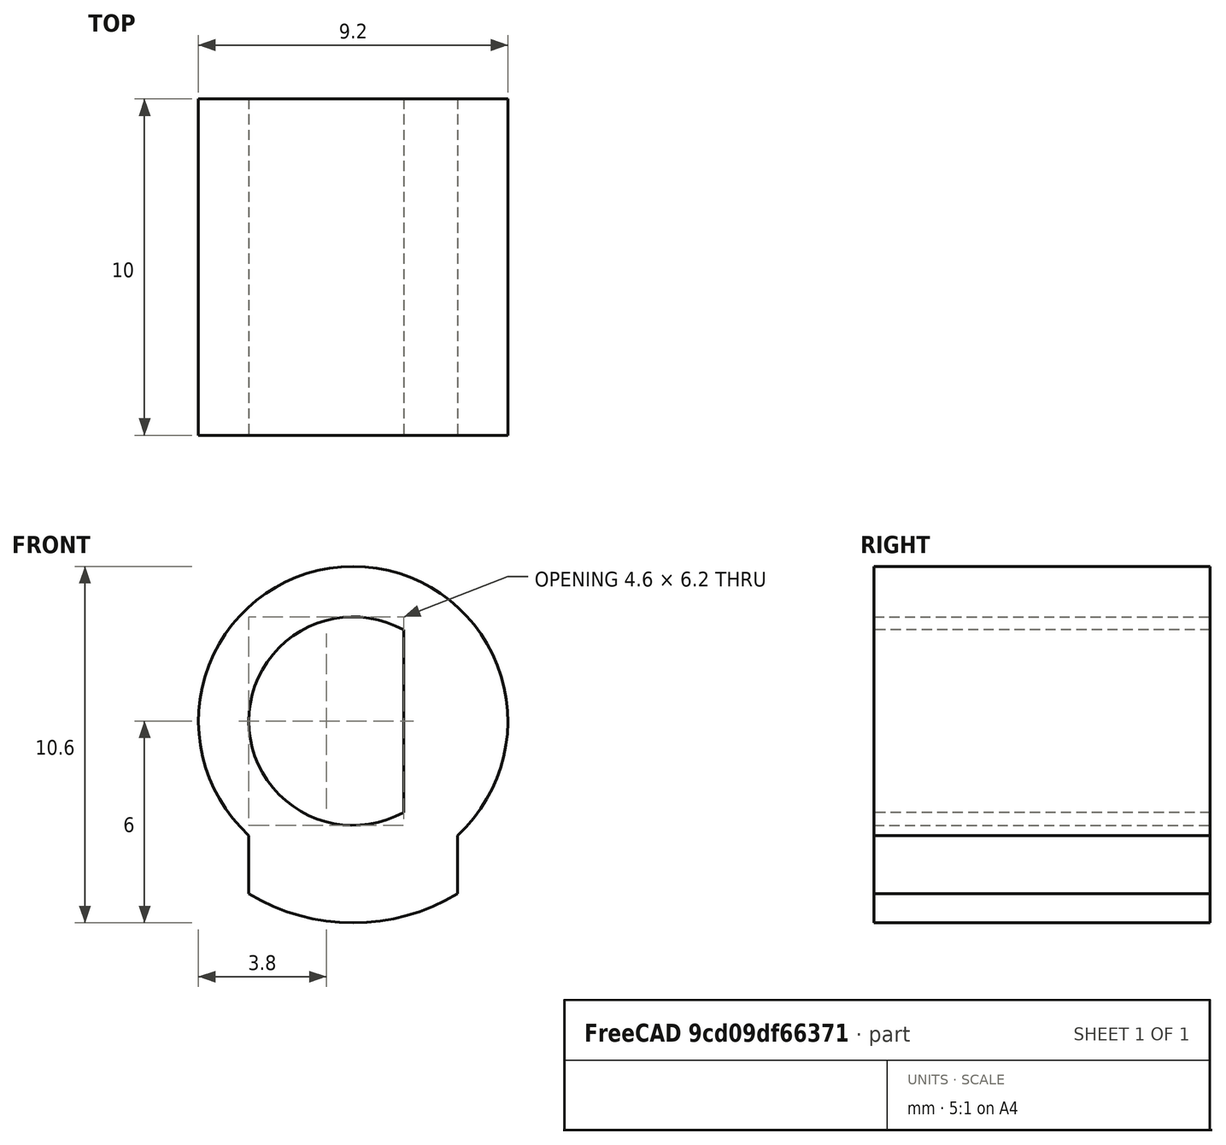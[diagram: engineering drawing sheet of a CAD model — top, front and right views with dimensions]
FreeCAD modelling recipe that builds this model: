
FCSTD DOCUMENT  (FreeCAD 0.19R24276 (Git))
Label: volume_knob
License: All rights reserved
LicenseURL: http://en.wikipedia.org/wiki/All_rights_reserved
objects: Spreadsheet::Sheet×1, Sketcher::SketchObject×1, PartDesign::Pad×1, PartDesign::Body×1
note: 4 computed .brp shape members not serialized (recipe doc carries the construction recipe); baked Part::Feature solids carry a one-line shape summary decoded from their .brp

FEATURE [Spreadsheet::Sheet] Spreadsheet
  cells = A1=overall diam; B1(overall_diam)=12; A2=shaft diam; B2(shaft_diam)=6.2; A3=shaft flat; B3(shaft_flat)=4.6; A4=shaft flat dist; B4(shaft_flat_offset)==shaft_flat - shaft_diam / 2; A5=shaft depth; B5(shaft_depth)=7
FEATURE [Sketcher::SketchObject] Sketch
  FullyConstrained = true
  MapMode = 5
  Placement = pos=(0,0,0) rot=(1,0,0;1.5708rad)
  Support = -> [XZ_Plane]
  expr: Constraints[15] = <<Spreadsheet>>.shaft_diam + 3
  expr: Constraints[9] = <<Spreadsheet>>.overall_diam
  expr: Constraints[7] = <<Spreadsheet>>.shaft_diam
  expr: Constraints[6] = <<Spreadsheet>>.shaft_flat_offset
  sketch-geometry (11):
    g0: Circle CenterX=0 CenterY=0 CenterZ=0 NormalX=0 NormalY=0 NormalZ=1 AngleXU=0 Radius=3.1
    g1: LineSegment StartX=1.5 StartY=2.71293 StartZ=0 EndX=1.5 EndY=-2.71293 EndZ=0
    g2: ArcOfCircle CenterX=0 CenterY=0 CenterZ=0 NormalX=0 NormalY=0 NormalZ=1 AngleXU=0 Radius=3.1 StartAngle=1.06572 EndAngle=5.21746
    g3: Circle CenterX=0 CenterY=0 CenterZ=0 NormalX=0 NormalY=0 NormalZ=1 AngleXU=0 Radius=6
    g4: LineSegment StartX=-3.1 StartY=0 StartZ=0 EndX=-3.1 EndY=-5.13712 EndZ=0
    g5: Circle CenterX=0 CenterY=0 CenterZ=0 NormalX=0 NormalY=0 NormalZ=1 AngleXU=0 Radius=4.6
    g6: LineSegment StartX=-3.1 StartY=-5.13712 StartZ=0 EndX=-3.1 EndY=-3.39853 EndZ=0
    g7: ArcOfCircle CenterX=0 CenterY=0 CenterZ=0 NormalX=0 NormalY=0 NormalZ=1 AngleXU=0 Radius=4.6 StartAngle=5.45188 EndAngle=10.2561
    g8: ArcOfCircle CenterX=0 CenterY=0 CenterZ=0 NormalX=0 NormalY=0 NormalZ=1 AngleXU=0 Radius=6 StartAngle=4.16944 EndAngle=5.25534
    g9: LineSegment StartX=3.1 StartY=5.69007e-08 StartZ=0 EndX=3.1 EndY=-5.13712 EndZ=0
    g10: LineSegment StartX=3.1 StartY=-5.13712 StartZ=0 EndX=3.1 EndY=-3.39853 EndZ=0
  constraints (31):
    c: Coincident(g0,g-1)
    c: PointOnObject(g1,g0)
    c: Vertical(g1)
    c: Coincident(g2,g-1)
    c: Coincident(g2,g1)
    c: Coincident(g2,g1)
    c: DistanceX(g2,g1) = 1.5
    c: Diameter(g0) = 6.2
    c: Coincident(g3,g2)
    c: Diameter(g3) = 12
    c: PointOnObject(g4,g2)
    c: PointOnObject(g4,g3)
    c: Vertical(g4)
    c: PointOnObject(g4,g-1)
    c: Coincident(g5,g2)
    c: Diameter(g5) = 9.2
    c: PointOnObject(g7,g5)
    c: Coincident(g6,g4)
    c: Coincident(g7,g2)
    c: Coincident(g7,g6)
    c: PointOnObject(g6,g4)
    c: Coincident(g8,g2)
    c: PointOnObject(g8,g6)
    c: PointOnObject(g9,g0)
    c: PointOnObject(g9,g3)
    c: Tangent(g9,g0)
    c: Vertical(g9)
    c: Coincident(g9,g8)
    c: Coincident(g10,g8)
    c: Coincident(g10,g7)
    c: PointOnObject(g7,g9)
FEATURE [PartDesign::Pad] Pad
  Direction = (1,1,1)
  Length = 10
  Length2 = 100
  Placement = pos=(0,0,0) rot=(1,0,0;1.5708rad)
  Profile = -> Sketch
  Type = 0
  expr: Length = <<Spreadsheet>>.shaft_depth + 3
FEATURE [PartDesign::Body] Body
  Group = -> [Sketch,Pad]
  Origin = -> Origin
  Tip = -> Pad
